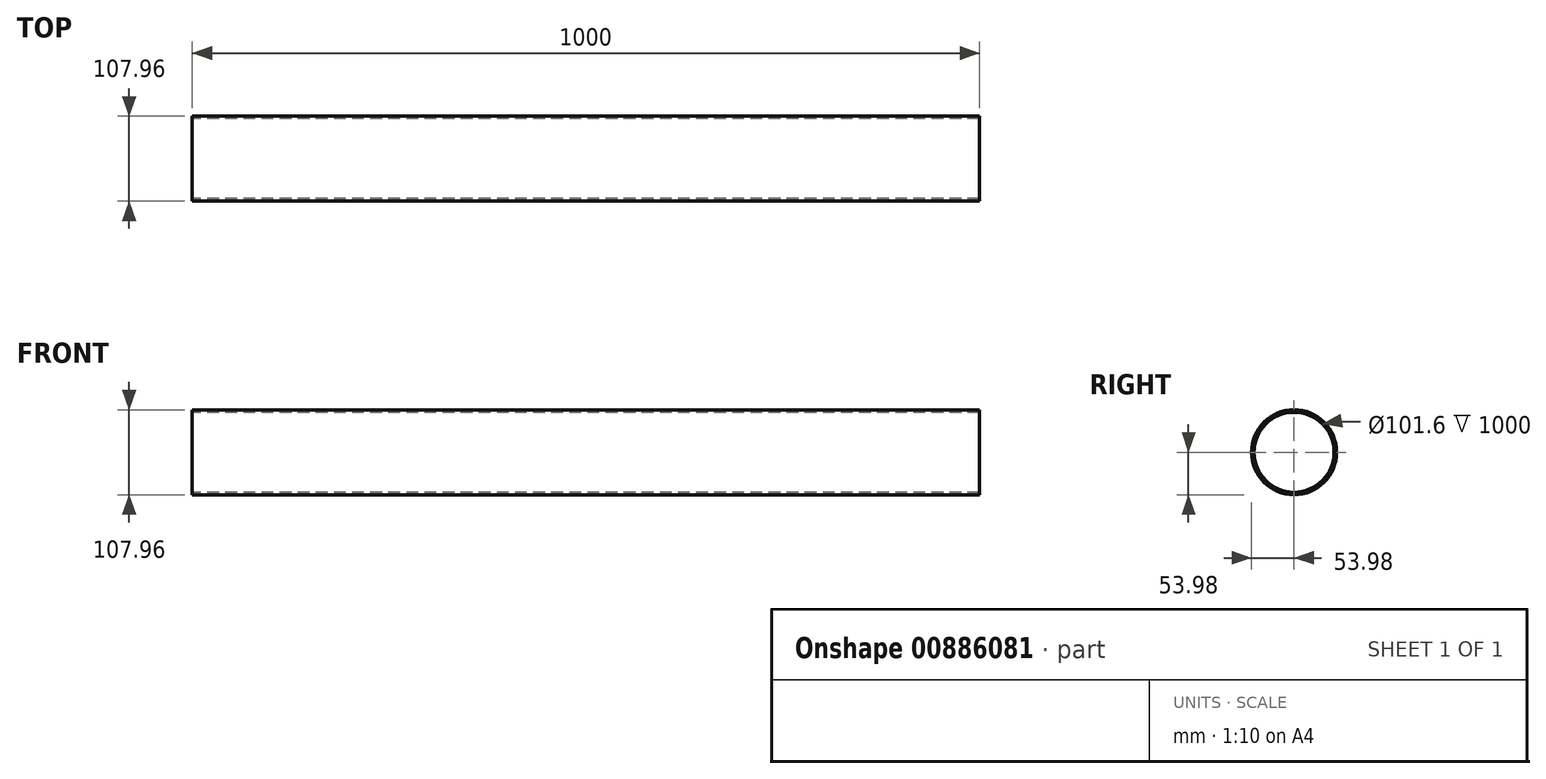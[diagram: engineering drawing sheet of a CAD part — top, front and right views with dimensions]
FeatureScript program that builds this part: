
annotation { "Feature Type Name" : "Feature", "Feature Type Description" : "" }
export const myFeature = defineFeature(function(context is Context, id is Id, definition is map)
    precondition{}
    {
        {
            var Q0;
            Q0=qCreatedBy(makeId("Right.planeOp"),FACE);
            var sketch = newSketch(context, id + "F0", { "sketchPlane" : qUnion([Q0])});
            skCircle(sketch, "E0", {"center": v(0, 0) * mm, "radius": 50.8 * mm});
            skCircle(sketch, "E1", {"center": v(0, 0) * mm, "radius": 53.98 * mm});
            skSolve(sketch);
        }
        {
            var Q0;
            Q0=qSketchRegion(id+"F0",true);
            extrude(context, id + "F1", {"entities" : qUnion([Q0]), "depth" : 1000 * mm, "offsetDistance" : 25 * mm});
        }
    });
